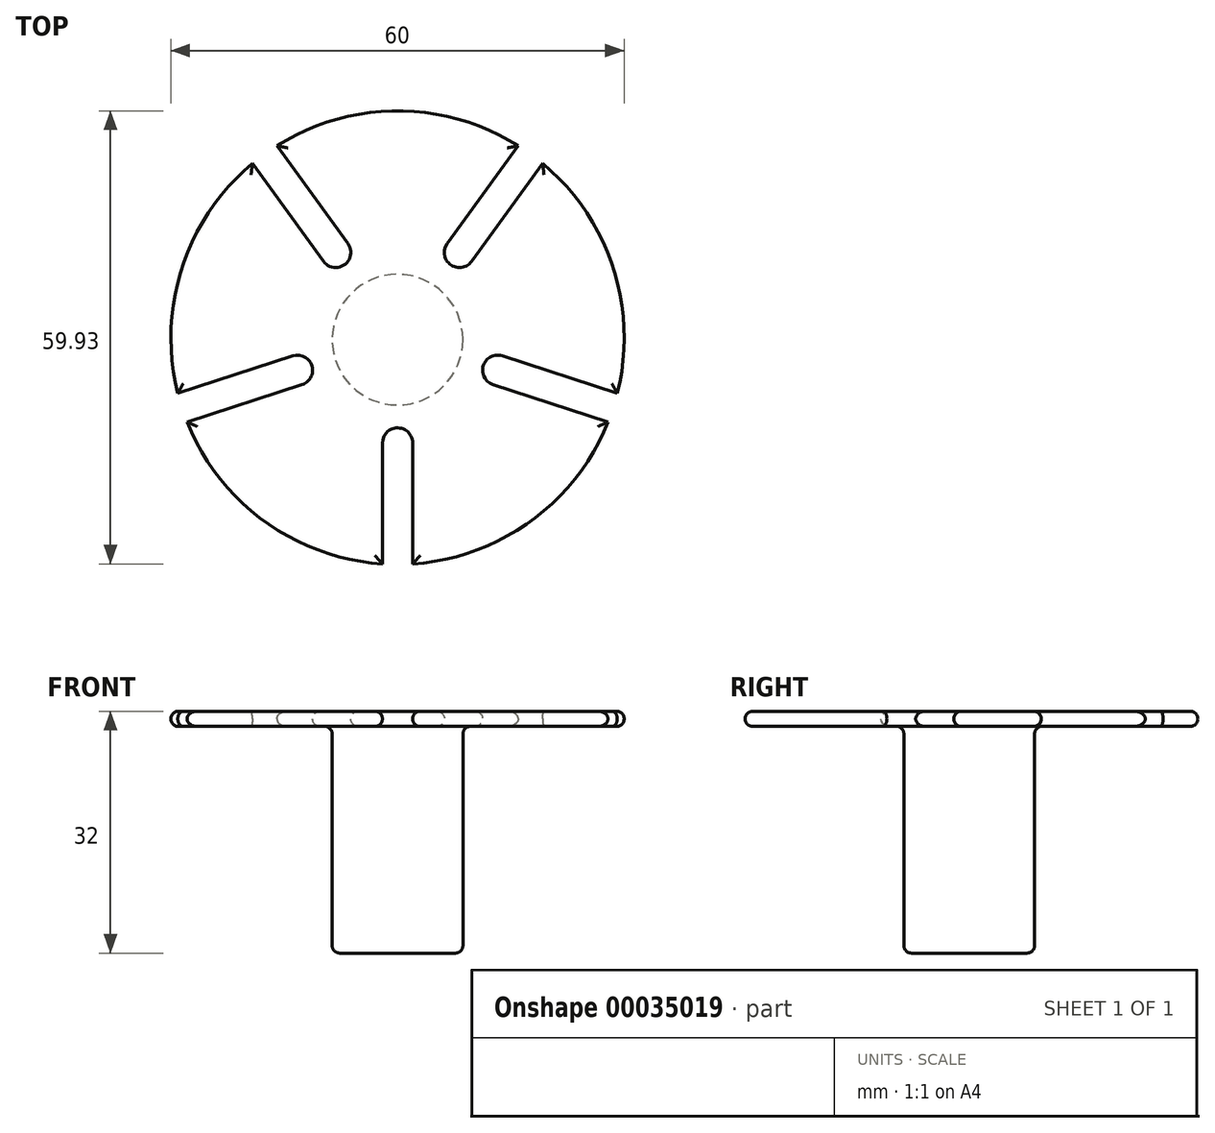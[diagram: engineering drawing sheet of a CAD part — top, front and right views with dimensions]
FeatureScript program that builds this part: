
annotation { "Feature Type Name" : "Feature", "Feature Type Description" : "" }
export const myFeature = defineFeature(function(context is Context, id is Id, definition is map)
    precondition{}
    {
        {
            var Q0;
            Q0=qCreatedBy(makeId("Top.planeOp"),FACE);
            var sketch = newSketch(context, id + "F0", { "sketchPlane" : qUnion([Q0])});
            skCircle(sketch, "E0", {"center": v(0, -0.26) * mm, "radius": 8.65 * mm});
            skSolve(sketch);
        }
        {
            var Q0;
            Q0=makeQuery(id+"F0.imprint","IMPRINT",FACE,{"disambiguationData":[TD([[makeQuery(id+"F0.imprint","IMPRINT",EDGE,{"derivedFrom":sQuery(id+"F0.wireOp",EDGE,"E0")}),1.0]])]});
            extrude(context, id + "F1", {"entities" : qUnion([Q0]), "depth" : 30 * mm});
        }
        {
            var Q0;
            Q0=makeQuery(id+"F1.opExtrude","CAP_FACE",FACE,{"disambiguationData":[OSD([sQuery(id+"F0.wireOp",EDGE,"E0")])],"isStart":false});
            var sketch = newSketch(context, id + "F2", { "sketchPlane" : qUnion([Q0])});
            skCircle(sketch, "E1", {"center": v(0, 0) * mm, "radius": 30 * mm});
            skSolve(sketch);
        }
        {
            var Q0;
            Q0=makeQuery(id+"F2.imprint","IMPRINT",FACE,{"disambiguationData":[TD([[makeQuery(id+"F2.imprint","IMPRINT",EDGE,{"derivedFrom":sQuery(id+"F2.wireOp",EDGE,"E1")}),1.0]])]});
            var Q1;
            Q1=makeQuery(id+"F2.imprint","IMPRINT",FACE,{"disambiguationData":[TD([[makeQuery(id+"F2.imprint","IMPRINT",EDGE,{"derivedFrom":makeQuery(id+"F1.opExtrude","CAP_EDGE",EDGE,{"disambiguationData":[OSD([sQuery(id+"F0.wireOp",EDGE,"E0")])],"isStart":false})}),1.0]])]});
            extrude(context, id + "F3", {"entities" : qUnion([Q0, Q1]), "operationType" : NewBodyOperationType.ADD, "depth" : 2 * mm});
        }
        {
            var Q0;
            Q0=makeQuery(id+"F3.opExtrude","CAP_FACE",FACE,{"disambiguationData":[OSD([sQuery(id+"F2.wireOp",EDGE,"E1")])],"isStart":false});
            var sketch = newSketch(context, id + "F4", { "sketchPlane" : qUnion([Q0])});
            skLineSegment(sketch, "E2", {"start": v(0, 0) * mm, "end": v(0, -30) * mm, "construction": true});
            skLineSegment(sketch, "E3", {"start": v(-2, -29.93) * mm, "end": v(-2, -13.93) * mm});
            skLineSegment(sketch, "E4", {"start": v(2, -29.93) * mm, "end": v(2, -13.93) * mm});
            skArc(sketch, "E5", {"start": v(2, -13.93) * mm, "mid": v(0, -11.93) * mm, "end": v(-2, -13.93) * mm});
            skLineSegment(sketch, "E6.1.0", {"start": v(29.09, -7.35) * mm, "end": v(13.87, -2.4) * mm});
            skArc(sketch, "E6.1.1", {"start": v(13.87, -2.4) * mm, "mid": v(11.35, -3.69) * mm, "end": v(12.63, -6.2) * mm});
            skLineSegment(sketch, "E6.1.2", {"start": v(27.85, -11.15) * mm, "end": v(12.63, -6.2) * mm});
            skLineSegment(sketch, "E6.2.0", {"start": v(15.98, 25.4) * mm, "end": v(6.57, 12.45) * mm});
            skArc(sketch, "E6.2.1", {"start": v(6.57, 12.45) * mm, "mid": v(7.01, 9.65) * mm, "end": v(9.8, 10.1) * mm});
            skLineSegment(sketch, "E6.2.2", {"start": v(19.21, 23.04) * mm, "end": v(9.8, 10.1) * mm});
            skLineSegment(sketch, "E6.3.0", {"start": v(-19.21, 23.04) * mm, "end": v(-9.8, 10.1) * mm});
            skArc(sketch, "E6.3.1", {"start": v(-9.8, 10.1) * mm, "mid": v(-7.01, 9.65) * mm, "end": v(-6.57, 12.45) * mm});
            skLineSegment(sketch, "E6.3.2", {"start": v(-15.98, 25.4) * mm, "end": v(-6.57, 12.45) * mm});
            skLineSegment(sketch, "E6.4.0", {"start": v(-27.85, -11.15) * mm, "end": v(-12.63, -6.2) * mm});
            skArc(sketch, "E6.4.1", {"start": v(-12.63, -6.2) * mm, "mid": v(-11.35, -3.69) * mm, "end": v(-13.87, -2.4) * mm});
            skLineSegment(sketch, "E6.4.2", {"start": v(-29.09, -7.35) * mm, "end": v(-13.87, -2.4) * mm});
            skPoint(sketch, "E6.center", {"position": v(0, 0) * mm});
            skSolve(sketch);
        }
        {
            var Q0;
            {var subQ2=sQuery(id+"F4.wireOp",EDGE,"E6.5.0");Q0=makeQuery(id+"F4.imprint","IMPRINT",FACE,{"disambiguationData":[TD([[makeQuery(id+"F4.imprint","IMPRINT",EDGE,{"derivedFrom":subQ2}),1.0]])]});}
            var Q1;
            {var subQ2=sQuery(id+"F4.wireOp",EDGE,"E6.6.0");Q1=makeQuery(id+"F4.imprint","IMPRINT",FACE,{"disambiguationData":[TD([[makeQuery(id+"F4.imprint","IMPRINT",EDGE,{"derivedFrom":subQ2}),1.0]])]});}
            var Q2;
            {var subQ2=sQuery(id+"F4.wireOp",EDGE,"E6.4.0");Q2=makeQuery(id+"F4.imprint","IMPRINT",FACE,{"disambiguationData":[TD([[makeQuery(id+"F4.imprint","IMPRINT",EDGE,{"derivedFrom":subQ2}),1.0]])]});}
            var Q3;
            {var subQ2=sQuery(id+"F4.wireOp",EDGE,"E6.3.0");Q3=makeQuery(id+"F4.imprint","IMPRINT",FACE,{"disambiguationData":[TD([[makeQuery(id+"F4.imprint","IMPRINT",EDGE,{"derivedFrom":subQ2}),1.0]])]});}
            var Q4;
            {var subQ2=sQuery(id+"F4.wireOp",EDGE,"E6.2.0");Q4=makeQuery(id+"F4.imprint","IMPRINT",FACE,{"disambiguationData":[TD([[makeQuery(id+"F4.imprint","IMPRINT",EDGE,{"derivedFrom":subQ2}),1.0]])]});}
            var Q5;
            {var subQ2=sQuery(id+"F4.wireOp",EDGE,"E6.1.0");Q5=makeQuery(id+"F4.imprint","IMPRINT",FACE,{"disambiguationData":[TD([[makeQuery(id+"F4.imprint","IMPRINT",EDGE,{"derivedFrom":subQ2}),1.0]])]});}
            var Q6;
            {var subQ2=sQuery(id+"F4.wireOp",EDGE,"E3");Q6=makeQuery(id+"F4.imprint","IMPRINT",FACE,{"disambiguationData":[TD([[makeQuery(id+"F4.imprint","IMPRINT",EDGE,{"derivedFrom":subQ2}),-1.0]])]});}
            var Q7;
            {var subQ2=sQuery(id+"F4.wireOp",EDGE,"E6.7.0");Q7=makeQuery(id+"F4.imprint","IMPRINT",FACE,{"disambiguationData":[TD([[makeQuery(id+"F4.imprint","IMPRINT",EDGE,{"derivedFrom":subQ2}),1.0]])]});}
            extrude(context, id + "F5", {"entities" : qUnion([Q0, Q1, Q2, Q3, Q4, Q5, Q6, Q7]), "operationType" : NewBodyOperationType.REMOVE, "endBound" : BoundingType.UP_TO_NEXT, "oppositeDirection" : true, "depth" : 25 * mm});
        }
        {
            var Q0;
            Q0=makeQuery(id+"F3.opExtrude","CAP_FACE",FACE,{"disambiguationData":[OSD([sQuery(id+"F2.wireOp",EDGE,"E1")])],"isStart":false});
            var Q1;
            Q1=makeQuery(id+"F3.opExtrude","CAP_FACE",FACE,{"disambiguationData":[OSD([sQuery(id+"F2.wireOp",EDGE,"E1")])],"isStart":true});
            var Q2;
            Q2=makeQuery(id+"F1.opExtrude","CAP_FACE",FACE,{"disambiguationData":[OSD([sQuery(id+"F0.wireOp",EDGE,"E0")])],"isStart":true});
            fillet(context, id + "F6", {"entities" : qUnion([Q0, Q1, Q2]), "radius" : 1 * mm, "tangentPropagation" : true, "allowEdgeOverflow" : false});
        }
    });
